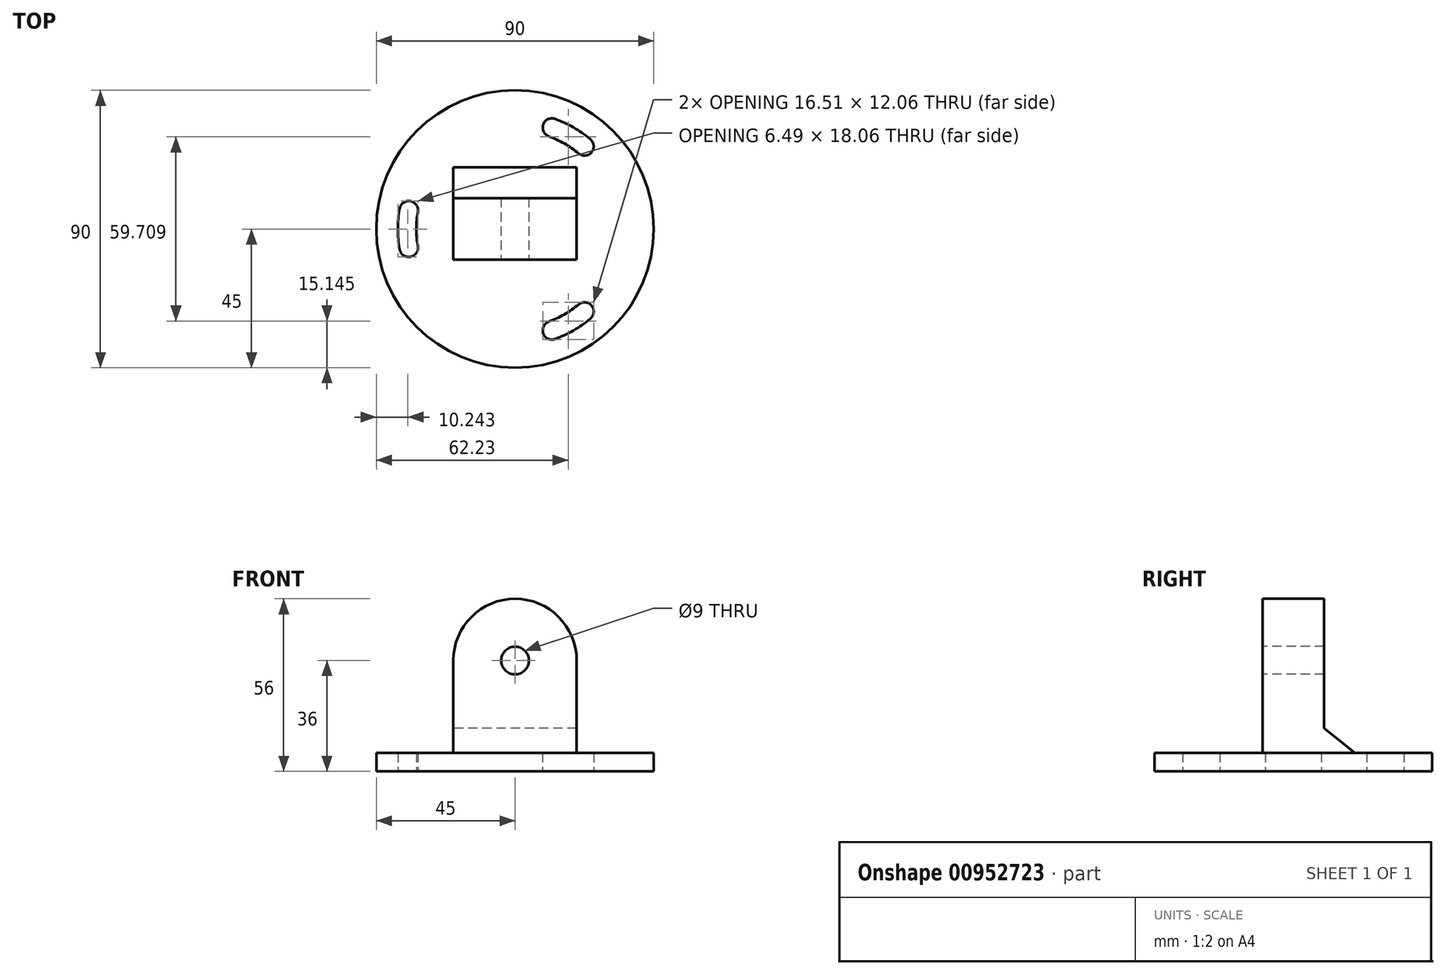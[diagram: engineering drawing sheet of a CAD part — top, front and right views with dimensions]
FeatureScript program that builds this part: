
annotation { "Feature Type Name" : "Feature", "Feature Type Description" : "" }
export const myFeature = defineFeature(function(context is Context, id is Id, definition is map)
    precondition{}
    {
        {
            var Q0;
            Q0=qCreatedBy(makeId("Top.planeOp"),FACE);
            var sketch = newSketch(context, id + "F0", { "sketchPlane" : qUnion([Q0])});
            skCircle(sketch, "E0", {"center": v(0, 0) * mm, "radius": 45 * mm});
            skCircle(sketch, "E1", {"center": v(0, 0) * mm, "radius": 35 * mm});
            skLineSegment(sketch, "E2", {"start": v(0, 0) * mm, "end": v(-45, 0) * mm});
            skLineSegment(sketch, "E3", {"start": v(0, 0) * mm, "end": v(22.5, 38.97) * mm});
            skLineSegment(sketch, "E4", {"start": v(0, 0) * mm, "end": v(22.5, -38.97) * mm});
            skLineSegment(sketch, "E5", {"start": v(0, 0) * mm, "end": v(15.4, 42.29) * mm});
            skLineSegment(sketch, "E6", {"start": v(0, 0) * mm, "end": v(28.93, 34.47) * mm});
            skLineSegment(sketch, "E7", {"start": v(0, 0) * mm, "end": v(28.93, -34.47) * mm});
            skLineSegment(sketch, "E8", {"start": v(0, 0) * mm, "end": v(15.4, -42.29) * mm});
            skLineSegment(sketch, "E9", {"start": v(0, 0) * mm, "end": v(-44.32, -7.81) * mm});
            skLineSegment(sketch, "E10", {"start": v(0, 0) * mm, "end": v(-44.32, 7.81) * mm});
            skCircle(sketch, "E11", {"center": v(0, 0) * mm, "radius": 32 * mm});
            skCircle(sketch, "E12", {"center": v(0, 0) * mm, "radius": 38 * mm});
            skCircle(sketch, "E13", {"center": v(11.97, 32.89) * mm, "radius": 3 * mm});
            skCircle(sketch, "E14", {"center": v(22.5, 26.81) * mm, "radius": 3 * mm});
            skCircle(sketch, "E15", {"center": v(22.5, -26.81) * mm, "radius": 3 * mm});
            skCircle(sketch, "E16", {"center": v(11.97, -32.89) * mm, "radius": 3 * mm});
            skCircle(sketch, "E17", {"center": v(-34.47, -6.08) * mm, "radius": 3 * mm});
            skCircle(sketch, "E18", {"center": v(-34.47, 6.08) * mm, "radius": 3 * mm});
            skSolve(sketch);
        }
        {
            var Q0;
            {var subQ0=sQuery(id+"F0.wireOp",EDGE,"E6");var subQ1=sQuery(id+"F0.wireOp",EDGE,"E0");var subQ2=makeQuery(id+"F0.imprint","INTERSECT",VERTEX,{"derivedFrom":[subQ1,subQ0]});Q0=makeQuery(id+"F0.imprint","IMPRINT",FACE,{"disambiguationData":[TD([[makeQuery(id+"F0.imprint","IMPRINT",EDGE,{"disambiguationData":[TD([[subQ2,1.0]])],"derivedFrom":subQ1}),1.0]])]});}
            var Q1;
            {var subQ0=sQuery(id+"F0.wireOp",EDGE,"E4");var subQ1=sQuery(id+"F0.wireOp",EDGE,"E0");var subQ2=makeQuery(id+"F0.imprint","INTERSECT",VERTEX,{"derivedFrom":[subQ1,subQ0]});Q1=makeQuery(id+"F0.imprint","IMPRINT",FACE,{"disambiguationData":[TD([[makeQuery(id+"F0.imprint","IMPRINT",EDGE,{"disambiguationData":[TD([[subQ2,-1.0]])],"derivedFrom":subQ1}),1.0]])]});}
            var Q2;
            {var subQ0=sQuery(id+"F0.wireOp",EDGE,"E4");var subQ1=sQuery(id+"F0.wireOp",EDGE,"E0");var subQ2=makeQuery(id+"F0.imprint","INTERSECT",VERTEX,{"derivedFrom":[subQ1,subQ0]});Q2=makeQuery(id+"F0.imprint","IMPRINT",FACE,{"disambiguationData":[TD([[makeQuery(id+"F0.imprint","IMPRINT",EDGE,{"disambiguationData":[TD([[subQ2,1.0]])],"derivedFrom":subQ1}),1.0]])]});}
            var Q3;
            {var subQ0=sQuery(id+"F0.wireOp",EDGE,"E8");var subQ1=sQuery(id+"F0.wireOp",EDGE,"E0");var subQ2=makeQuery(id+"F0.imprint","INTERSECT",VERTEX,{"derivedFrom":[subQ1,subQ0]});Q3=makeQuery(id+"F0.imprint","IMPRINT",FACE,{"disambiguationData":[TD([[makeQuery(id+"F0.imprint","IMPRINT",EDGE,{"disambiguationData":[TD([[subQ2,1.0]])],"derivedFrom":subQ1}),1.0]])]});}
            var Q4;
            {var subQ0=sQuery(id+"F0.wireOp",EDGE,"E17");var subQ1=sQuery(id+"F0.wireOp",EDGE,"E1");var subQ2=makeQuery(id+"F0.imprint","INTERSECT",VERTEX,{"disambiguationData":[OD(1.0)],"derivedFrom":[subQ1,subQ0]});Q4=makeQuery(id+"F0.imprint","IMPRINT",FACE,{"disambiguationData":[TD([[makeQuery(id+"F0.imprint","IMPRINT",EDGE,{"disambiguationData":[TD([[subQ2,-1.0]])],"derivedFrom":subQ1}),-1.0]])]});}
            var Q5;
            {var subQ0=sQuery(id+"F0.wireOp",EDGE,"E17");var subQ1=sQuery(id+"F0.wireOp",EDGE,"E1");var subQ2=makeQuery(id+"F0.imprint","INTERSECT",VERTEX,{"disambiguationData":[OD(1.0)],"derivedFrom":[subQ1,subQ0]});Q5=makeQuery(id+"F0.imprint","IMPRINT",FACE,{"disambiguationData":[TD([[makeQuery(id+"F0.imprint","IMPRINT",EDGE,{"disambiguationData":[TD([[subQ2,-1.0]])],"derivedFrom":subQ1}),1.0]])]});}
            var Q6;
            {var subQ1=sQuery(id+"F0.wireOp",EDGE,"E8");var subQ3=sQuery(id+"F0.wireOp",EDGE,"E11");var subQ4=makeQuery(id+"F0.imprint","INTERSECT",VERTEX,{"derivedFrom":[subQ1,subQ3,sQuery(id+"F0.wireOp",EDGE,"E16")]});Q6=makeQuery(id+"F0.imprint","IMPRINT",FACE,{"disambiguationData":[TD([[makeQuery(id+"F0.imprint","IMPRINT",EDGE,{"disambiguationData":[TD([[subQ4,1.0]])],"derivedFrom":subQ3}),1.0]])]});}
            var Q7;
            {var subQ1=sQuery(id+"F0.wireOp",EDGE,"E2");var subQ3=sQuery(id+"F0.wireOp",EDGE,"E11");var subQ4=makeQuery(id+"F0.imprint","INTERSECT",VERTEX,{"derivedFrom":[subQ1,subQ3]});Q7=makeQuery(id+"F0.imprint","IMPRINT",FACE,{"disambiguationData":[TD([[makeQuery(id+"F0.imprint","IMPRINT",EDGE,{"disambiguationData":[TD([[subQ4,-1.0]])],"derivedFrom":subQ3}),1.0]])]});}
            var Q8;
            {var subQ1=sQuery(id+"F0.wireOp",EDGE,"E2");var subQ3=sQuery(id+"F0.wireOp",EDGE,"E11");var subQ4=makeQuery(id+"F0.imprint","INTERSECT",VERTEX,{"derivedFrom":[subQ1,subQ3]});Q8=makeQuery(id+"F0.imprint","IMPRINT",FACE,{"disambiguationData":[TD([[makeQuery(id+"F0.imprint","IMPRINT",EDGE,{"disambiguationData":[TD([[subQ4,1.0]])],"derivedFrom":subQ3}),1.0]])]});}
            var Q9;
            {var subQ0=sQuery(id+"F0.wireOp",EDGE,"E2");var subQ1=sQuery(id+"F0.wireOp",EDGE,"E0");var subQ2=makeQuery(id+"F0.imprint","INTERSECT",VERTEX,{"derivedFrom":[subQ1,subQ0]});Q9=makeQuery(id+"F0.imprint","IMPRINT",FACE,{"disambiguationData":[TD([[makeQuery(id+"F0.imprint","IMPRINT",EDGE,{"disambiguationData":[TD([[subQ2,-1.0]])],"derivedFrom":subQ1}),1.0]])]});}
            var Q10;
            {var subQ0=sQuery(id+"F0.wireOp",EDGE,"E2");var subQ1=sQuery(id+"F0.wireOp",EDGE,"E0");var subQ2=makeQuery(id+"F0.imprint","INTERSECT",VERTEX,{"derivedFrom":[subQ1,subQ0]});Q10=makeQuery(id+"F0.imprint","IMPRINT",FACE,{"disambiguationData":[TD([[makeQuery(id+"F0.imprint","IMPRINT",EDGE,{"disambiguationData":[TD([[subQ2,1.0]])],"derivedFrom":subQ1}),1.0]])]});}
            var Q11;
            {var subQ0=sQuery(id+"F0.wireOp",EDGE,"E5");var subQ1=sQuery(id+"F0.wireOp",EDGE,"E0");var subQ2=makeQuery(id+"F0.imprint","INTERSECT",VERTEX,{"derivedFrom":[subQ1,subQ0]});Q11=makeQuery(id+"F0.imprint","IMPRINT",FACE,{"disambiguationData":[TD([[makeQuery(id+"F0.imprint","IMPRINT",EDGE,{"disambiguationData":[TD([[subQ2,-1.0]])],"derivedFrom":subQ1}),1.0]])]});}
            var Q12;
            {var subQ0=sQuery(id+"F0.wireOp",EDGE,"E13");var subQ1=sQuery(id+"F0.wireOp",EDGE,"E1");var subQ2=makeQuery(id+"F0.imprint","INTERSECT",VERTEX,{"disambiguationData":[OD(1.0)],"derivedFrom":[subQ1,subQ0]});Q12=makeQuery(id+"F0.imprint","IMPRINT",FACE,{"disambiguationData":[TD([[makeQuery(id+"F0.imprint","IMPRINT",EDGE,{"disambiguationData":[TD([[subQ2,-1.0]])],"derivedFrom":subQ1}),-1.0]])]});}
            var Q13;
            {var subQ1=sQuery(id+"F0.wireOp",EDGE,"E5");var subQ3=sQuery(id+"F0.wireOp",EDGE,"E11");var subQ4=makeQuery(id+"F0.imprint","INTERSECT",VERTEX,{"derivedFrom":[subQ1,subQ3,sQuery(id+"F0.wireOp",EDGE,"E13")]});Q13=makeQuery(id+"F0.imprint","IMPRINT",FACE,{"disambiguationData":[TD([[makeQuery(id+"F0.imprint","IMPRINT",EDGE,{"disambiguationData":[TD([[subQ4,-1.0]])],"derivedFrom":subQ3}),1.0]])]});}
            var Q14;
            {var subQ0=sQuery(id+"F0.wireOp",EDGE,"E13");var subQ1=sQuery(id+"F0.wireOp",EDGE,"E1");var subQ2=makeQuery(id+"F0.imprint","INTERSECT",VERTEX,{"disambiguationData":[OD(1.0)],"derivedFrom":[subQ1,subQ0]});Q14=makeQuery(id+"F0.imprint","IMPRINT",FACE,{"disambiguationData":[TD([[makeQuery(id+"F0.imprint","IMPRINT",EDGE,{"disambiguationData":[TD([[subQ2,-1.0]])],"derivedFrom":subQ1}),1.0]])]});}
            var Q15;
            {var subQ0=sQuery(id+"F0.wireOp",EDGE,"E3");var subQ1=sQuery(id+"F0.wireOp",EDGE,"E0");var subQ2=makeQuery(id+"F0.imprint","INTERSECT",VERTEX,{"derivedFrom":[subQ1,subQ0]});Q15=makeQuery(id+"F0.imprint","IMPRINT",FACE,{"disambiguationData":[TD([[makeQuery(id+"F0.imprint","IMPRINT",EDGE,{"disambiguationData":[TD([[subQ2,-1.0]])],"derivedFrom":subQ1}),1.0]])]});}
            var Q16;
            {var subQ0=sQuery(id+"F0.wireOp",EDGE,"E3");var subQ1=sQuery(id+"F0.wireOp",EDGE,"E0");var subQ2=makeQuery(id+"F0.imprint","INTERSECT",VERTEX,{"derivedFrom":[subQ1,subQ0]});Q16=makeQuery(id+"F0.imprint","IMPRINT",FACE,{"disambiguationData":[TD([[makeQuery(id+"F0.imprint","IMPRINT",EDGE,{"disambiguationData":[TD([[subQ2,1.0]])],"derivedFrom":subQ1}),1.0]])]});}
            var Q17;
            {var subQ1=sQuery(id+"F0.wireOp",EDGE,"E3");var subQ3=sQuery(id+"F0.wireOp",EDGE,"E11");var subQ4=makeQuery(id+"F0.imprint","INTERSECT",VERTEX,{"derivedFrom":[subQ1,subQ3]});Q17=makeQuery(id+"F0.imprint","IMPRINT",FACE,{"disambiguationData":[TD([[makeQuery(id+"F0.imprint","IMPRINT",EDGE,{"disambiguationData":[TD([[subQ4,1.0]])],"derivedFrom":subQ3}),1.0]])]});}
            var Q18;
            {var subQ1=sQuery(id+"F0.wireOp",EDGE,"E3");var subQ3=sQuery(id+"F0.wireOp",EDGE,"E11");var subQ4=makeQuery(id+"F0.imprint","INTERSECT",VERTEX,{"derivedFrom":[subQ1,subQ3]});Q18=makeQuery(id+"F0.imprint","IMPRINT",FACE,{"disambiguationData":[TD([[makeQuery(id+"F0.imprint","IMPRINT",EDGE,{"disambiguationData":[TD([[subQ4,-1.0]])],"derivedFrom":subQ3}),1.0]])]});}
            var Q19;
            {var subQ1=sQuery(id+"F0.wireOp",EDGE,"E6");var subQ3=sQuery(id+"F0.wireOp",EDGE,"E11");var subQ4=makeQuery(id+"F0.imprint","INTERSECT",VERTEX,{"derivedFrom":[subQ1,subQ3,sQuery(id+"F0.wireOp",EDGE,"E14")]});Q19=makeQuery(id+"F0.imprint","IMPRINT",FACE,{"disambiguationData":[TD([[makeQuery(id+"F0.imprint","IMPRINT",EDGE,{"disambiguationData":[TD([[subQ4,1.0]])],"derivedFrom":subQ3}),1.0]])]});}
            var Q20;
            {var subQ1=sQuery(id+"F0.wireOp",EDGE,"E4");var subQ3=sQuery(id+"F0.wireOp",EDGE,"E11");var subQ4=makeQuery(id+"F0.imprint","INTERSECT",VERTEX,{"derivedFrom":[subQ1,subQ3]});Q20=makeQuery(id+"F0.imprint","IMPRINT",FACE,{"disambiguationData":[TD([[makeQuery(id+"F0.imprint","IMPRINT",EDGE,{"disambiguationData":[TD([[subQ4,-1.0]])],"derivedFrom":subQ3}),1.0]])]});}
            var Q21;
            {var subQ1=sQuery(id+"F0.wireOp",EDGE,"E4");var subQ3=sQuery(id+"F0.wireOp",EDGE,"E11");var subQ4=makeQuery(id+"F0.imprint","INTERSECT",VERTEX,{"derivedFrom":[subQ1,subQ3]});Q21=makeQuery(id+"F0.imprint","IMPRINT",FACE,{"disambiguationData":[TD([[makeQuery(id+"F0.imprint","IMPRINT",EDGE,{"disambiguationData":[TD([[subQ4,1.0]])],"derivedFrom":subQ3}),1.0]])]});}
            var Q22;
            {var subQ0=sQuery(id+"F0.wireOp",EDGE,"E14");var subQ1=sQuery(id+"F0.wireOp",EDGE,"E1");var subQ2=makeQuery(id+"F0.imprint","INTERSECT",VERTEX,{"disambiguationData":[OD(0.0)],"derivedFrom":[subQ1,subQ0]});Q22=makeQuery(id+"F0.imprint","IMPRINT",FACE,{"disambiguationData":[TD([[makeQuery(id+"F0.imprint","IMPRINT",EDGE,{"disambiguationData":[TD([[subQ2,1.0]])],"derivedFrom":subQ1}),1.0]])]});}
            var Q23;
            {var subQ0=sQuery(id+"F0.wireOp",EDGE,"E14");var subQ1=sQuery(id+"F0.wireOp",EDGE,"E1");var subQ2=makeQuery(id+"F0.imprint","INTERSECT",VERTEX,{"disambiguationData":[OD(0.0)],"derivedFrom":[subQ1,subQ0]});Q23=makeQuery(id+"F0.imprint","IMPRINT",FACE,{"disambiguationData":[TD([[makeQuery(id+"F0.imprint","IMPRINT",EDGE,{"disambiguationData":[TD([[subQ2,1.0]])],"derivedFrom":subQ1}),-1.0]])]});}
            extrude(context, id + "F1", {"entities" : qUnion([Q0, Q1, Q2, Q3, Q4, Q5, Q6, Q7, Q8, Q9, Q10, Q11, Q12, Q13, Q14, Q15, Q16, Q17, Q18, Q19, Q20, Q21, Q22, Q23]), "depth" : 6 * mm, "offsetDistance" : 25 * mm});
        }
        {
            var Q0;
            Q0=makeQuery(id+"F1.opExtrude","CAP_FACE",FACE,{"disambiguationData":[OSD([sQuery(id+"F0.wireOp",EDGE,"E0"),sQuery(id+"F0.wireOp",EDGE,"E11"),sQuery(id+"F0.wireOp",EDGE,"E12"),sQuery(id+"F0.wireOp",EDGE,"E13"),sQuery(id+"F0.wireOp",EDGE,"E14"),sQuery(id+"F0.wireOp",EDGE,"E15"),sQuery(id+"F0.wireOp",EDGE,"E16"),sQuery(id+"F0.wireOp",EDGE,"E17"),sQuery(id+"F0.wireOp",EDGE,"E18")])],"isStart":false});
            var sketch = newSketch(context, id + "F2", { "sketchPlane" : qUnion([Q0])});
            skLineSegment(sketch, "E19.bottom", {"start": v(-20, 10) * mm, "end": v(20, 10) * mm});
            skLineSegment(sketch, "E19.top", {"start": v(-20, -10) * mm, "end": v(20, -10) * mm});
            skLineSegment(sketch, "E19.left", {"start": v(-20, 10) * mm, "end": v(-20, -10) * mm});
            skLineSegment(sketch, "E19.right", {"start": v(20, 10) * mm, "end": v(20, -10) * mm});
            skSolve(sketch);
        }
        {
            var Q0;
            Q0=makeQuery(id+"F2.imprint","IMPRINT",FACE,{"disambiguationData":[TD([[makeQuery(id+"F2.imprint","IMPRINT",EDGE,{"derivedFrom":sQuery(id+"F2.wireOp",EDGE,"E19.bottom")}),-1.0]])]});
            extrude(context, id + "F3", {"entities" : qUnion([Q0]), "operationType" : NewBodyOperationType.ADD, "depth" : 50 * mm, "offsetDistance" : 25 * mm});
        }
        {
            var Q0;
            Q0=makeQuery(id+"F3.opExtrude","SWEPT_FACE",FACE,{"disambiguationData":[OSD([sQuery(id+"F2.wireOp",EDGE,"E19.left")])]});
            var sketch = newSketch(context, id + "F4", { "sketchPlane" : qUnion([Q0])});
            skLineSegment(sketch, "E20.0", {"start": v(-45, 6) * mm, "end": v(45, 6) * mm});
            skLineSegment(sketch, "E21", {"start": v(-10, 6) * mm, "end": v(-10, 14) * mm});
            skLineSegment(sketch, "E22", {"start": v(-10, 14) * mm, "end": v(-20, 6) * mm});
            skLineSegment(sketch, "E23", {"start": v(-20, 6) * mm, "end": v(-10, 6) * mm});
            skLineSegment(sketch, "E24", {"start": v(10, 6) * mm, "end": v(18, 6) * mm});
            skLineSegment(sketch, "E25", {"start": v(18, 6) * mm, "end": v(10, 14) * mm});
            skLineSegment(sketch, "E26", {"start": v(10, 14) * mm, "end": v(10, 6) * mm});
            skSolve(sketch);
        }
        {
            var Q0;
            Q0=makeQuery(id+"F4.imprint","IMPRINT",FACE,{"disambiguationData":[TD([[makeQuery(id+"F4.imprint","IMPRINT",EDGE,{"derivedFrom":sQuery(id+"F4.wireOp",EDGE,"E24")}),1.0]])]});
            var Q1;
            Q1=makeQuery(id+"F4.imprint","IMPRINT",FACE,{"disambiguationData":[TD([[makeQuery(id+"F4.imprint","IMPRINT",EDGE,{"derivedFrom":sQuery(id+"F4.wireOp",EDGE,"E21")}),-1.0]])]});
            extrude(context, id + "F5", {"entities" : qUnion([Q0, Q1]), "operationType" : NewBodyOperationType.ADD, "depth" : -40 * mm, "offsetDistance" : 25 * mm});
        }
        {
            var Q0;
            Q0=makeQuery(id+"F3.opExtrude","SWEPT_FACE",FACE,{"disambiguationData":[OSD([sQuery(id+"F2.wireOp",EDGE,"E19.top")])]});
            var sketch = newSketch(context, id + "F6", { "sketchPlane" : qUnion([Q0])});
            skLineSegment(sketch, "E27", {"start": v(-20, 56) * mm, "end": v(0, 36) * mm});
            skLineSegment(sketch, "E28", {"start": v(0, 36) * mm, "end": v(20, 56) * mm});
            skCircle(sketch, "E29", {"center": v(0, 36) * mm, "radius": 20 * mm});
            skCircle(sketch, "E30", {"center": v(0, 36) * mm, "radius": 4.5 * mm});
            skSolve(sketch);
        }
        {
            var Q0;
            {var subQ0=sQuery(id+"F6.wireOp",EDGE,"E27");var subQ4=sQuery(id+"F6.wireOp",EDGE,"E29");var subQ5=makeQuery(id+"F6.imprint","INTERSECT",VERTEX,{"derivedFrom":[subQ0,subQ4]});Q0=makeQuery(id+"F6.imprint","IMPRINT",FACE,{"disambiguationData":[TD([[makeQuery(id+"F6.imprint","IMPRINT",EDGE,{"disambiguationData":[TD([[subQ5,-1.0]])],"derivedFrom":subQ4}),-1.0]])]});}
            var Q1;
            {var subQ0=sQuery(id+"F6.wireOp",EDGE,"E27");var subQ4=sQuery(id+"F6.wireOp",EDGE,"E29");var subQ5=makeQuery(id+"F6.imprint","INTERSECT",VERTEX,{"derivedFrom":[subQ0,subQ4]});Q1=makeQuery(id+"F6.imprint","IMPRINT",FACE,{"disambiguationData":[TD([[makeQuery(id+"F6.imprint","IMPRINT",EDGE,{"disambiguationData":[TD([[subQ5,1.0]])],"derivedFrom":subQ4}),-1.0]])]});}
            var Q2;
            {var subQ0=sQuery(id+"F6.wireOp",EDGE,"E28");var subQ4=sQuery(id+"F6.wireOp",EDGE,"E29");var subQ5=makeQuery(id+"F6.imprint","INTERSECT",VERTEX,{"derivedFrom":[subQ0,subQ4]});Q2=makeQuery(id+"F6.imprint","IMPRINT",FACE,{"disambiguationData":[TD([[makeQuery(id+"F6.imprint","IMPRINT",EDGE,{"disambiguationData":[TD([[subQ5,-1.0]])],"derivedFrom":subQ4}),-1.0]])]});}
            var Q3;
            {var subQ0=sQuery(id+"F6.wireOp",EDGE,"E28");var subQ4=sQuery(id+"F6.wireOp",EDGE,"E29");var subQ5=makeQuery(id+"F6.imprint","INTERSECT",VERTEX,{"derivedFrom":[subQ0,subQ4]});Q3=makeQuery(id+"F6.imprint","IMPRINT",FACE,{"disambiguationData":[TD([[makeQuery(id+"F6.imprint","IMPRINT",EDGE,{"disambiguationData":[TD([[subQ5,1.0]])],"derivedFrom":subQ4}),-1.0]])]});}
            extrude(context, id + "F7", {"entities" : qUnion([Q0, Q1, Q2, Q3]), "operationType" : NewBodyOperationType.REMOVE, "oppositeDirection" : true, "depth" : 30 * mm, "offsetDistance" : 25 * mm});
        }
        {
            var Q0;
            {var subQ0=sQuery(id+"F6.wireOp",EDGE,"E28");var subQ1=sQuery(id+"F6.wireOp",EDGE,"E27");var subQ2=makeQuery(id+"F6.imprint","INTERSECT",VERTEX,{"derivedFrom":[subQ1,subQ0]});Q0=makeQuery(id+"F6.imprint","IMPRINT",FACE,{"disambiguationData":[TD([[makeQuery(id+"F6.imprint","IMPRINT",EDGE,{"disambiguationData":[TD([[subQ2,1.0]])],"derivedFrom":subQ1}),-1.0]])]});}
            var Q1;
            {var subQ0=sQuery(id+"F6.wireOp",EDGE,"E28");var subQ1=sQuery(id+"F6.wireOp",EDGE,"E27");var subQ2=makeQuery(id+"F6.imprint","INTERSECT",VERTEX,{"derivedFrom":[subQ1,subQ0]});Q1=makeQuery(id+"F6.imprint","IMPRINT",FACE,{"disambiguationData":[TD([[makeQuery(id+"F6.imprint","IMPRINT",EDGE,{"disambiguationData":[TD([[subQ2,1.0]])],"derivedFrom":subQ1}),1.0]])]});}
            extrude(context, id + "F8", {"entities" : qUnion([Q0, Q1]), "operationType" : NewBodyOperationType.REMOVE, "oppositeDirection" : true, "depth" : 30 * mm, "offsetDistance" : 25 * mm});
        }
    });
